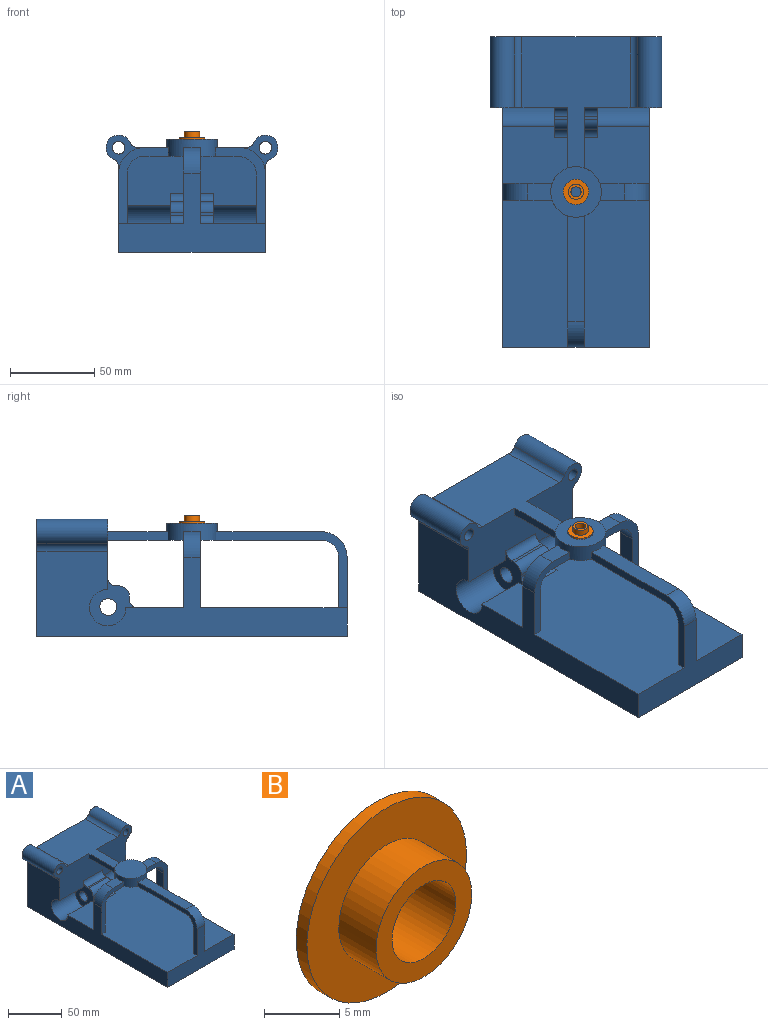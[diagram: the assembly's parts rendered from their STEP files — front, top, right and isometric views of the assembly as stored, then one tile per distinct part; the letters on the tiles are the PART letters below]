
ASSEMBLY  parts=2 mates=2
PART A: 49 faces, bbox 102x184x69.5 mm
  f0: plane 35.86x5mm, normal (1,0,0), area 179.3mm2, adj f4,f19,f30,f47
  f1: plane 35.86x5mm, normal (-1,0,0), area 179.3mm2, adj f4,f19,f30,f47
  f2: plane 62.86x10mm, normal (0,0,1), area 622.8mm2, adj f5,f6,f31,f47
  f3: plane 14.36x10mm, normal (0,0,1), area 137.8mm2, adj f7,f8,f41,f47
  f4: plane 77.86x64.09mm, normal (0,0,1), area 3044.5mm2, adj f0,f1,f15,f19,f38,f40,f47
  f5: plane 77.86x45mm, normal (1,0,0), area 562.5mm2, adj f2,f11,f17,f29,f30,f31,f32,f47
  f6: plane 77.86x45mm, normal (-1,0,0), area 562.5mm2, adj f2,f11,f17,f29,f30,f31,f32,f47
  f7: plane 45x29.36mm, normal (0,-1,0), area 320mm2, adj f3,f11,f16,f30,f41,f42,f43,f47
  f8: plane 45x29.36mm, normal (0,1,0), area 320mm2, adj f3,f11,f16,f30,f41,f42,f43,f47
  f9: plane 45x29.36mm, normal (0,-1,0), area 328.3mm2, adj f11,f12,f13,f30,f44,f45,f46,f47
  f10: plane 45x29.36mm, normal (0,1,0), area 328.3mm2, adj f11,f12,f13,f30,f44,f45,f46,f47
  f11: plane 131.18x87mm, normal (0,0,1), area 11087.4mm2, adj f5,f6,f7,f8,f9,f10,f12,f14
  f12: plane 184x50.54mm, normal (1,0,0), area 4560.9mm2, adj f9,f10,f11,f15,f17,f18,f19,f20
  f13: plane 14.36x10mm, normal (0,0,1), area 137.8mm2, adj f9,f10,f46,f47
  f14: cylinder r=10.82mm len=31mm, axis (1,0,0), area 1581mm2, adj f11,f16,f19,f24
  f15: plane 102x69.5mm, normal (0,1,0), area 5581mm2, adj f4,f12,f16,f18,f33,f34,f35,f36
  f16: plane 184x50.54mm, normal (-1,0,0), area 4560.9mm2, adj f7,f8,f11,f14,f15,f17,f18,f19
  f17: plane 87x47mm, normal (0,-1,0), area 1779mm2, adj f5,f6,f11,f12,f16,f18,f31
  f18: plane 184x87mm, normal (0,0,-1), area 16008mm2, adj f12,f15,f16,f17
  f19: plane 102x41.68mm, normal (0,-1,0), area 2935.5mm2, adj f0,f1,f4,f12,f14,f16,f20,f23
  f20: cylinder r=10.82mm len=31mm, axis (1,0,0), area 1581mm2, adj f11,f12,f19,f23
  f21: plane 25x1.82mm, normal (0,0,1), area 45.6mm2, adj f23,f24,f26,f27
  f22: plane 25x1.82mm, normal (0,-1,0), area 45.6mm2, adj f23,f24,f25,f27
  f23: plane 28.65x28.65mm, normal (1,0,0), area 364.8mm2, adj f11,f19,f20,f21,f22,f25,f26,f27
  f24: plane 28.65x28.65mm, normal (-1,0,0), area 364.8mm2, adj f11,f14,f19,f21,f22,f25,f26,f27
  f25: cylinder r=5mm len=25mm, axis (-1,0,0), area 196.3mm2, adj f11,f22,f23,f24
  f26: cylinder r=5mm len=25mm, axis (1,0,0), area 196.3mm2, adj f19,f21,f23,f24
  f27: cylinder r=6mm len=25mm, axis (1,0,0), area 235.6mm2, adj f21,f22,f23,f24
  f28: cylinder r=5mm len=25mm, axis (1,0,0), area 785.4mm2, adj f23,f24
  f29: cylinder r=10mm len=10mm, axis (-1,0,0), area 157.1mm2, adj f5,f6,f30,f32
  f30: plane 127x55.21mm, normal (0,0,-1), area 1940.2mm2, adj f0,f1,f5,f6,f7,f8,f9,f10
  f31: cylinder r=15mm len=15mm, axis (-1,0,0), area 235.6mm2, adj f2,f5,f6,f17
  f32: plane 30x10mm, normal (0,1,0), area 300mm2, adj f5,f6,f11,f29
  f33: cylinder r=7.5mm len=42mm, axis (0,-1,0), area 1225.1mm2, adj f15,f19,f39,f40
  f34: cylinder r=3.75mm len=42mm, axis (0,-1,0), area 989.6mm2, adj f15,f19
  f35: cylinder r=7.5mm len=42mm, axis (0,-1,0), area 1225.1mm2, adj f15,f19,f37,f38
  f36: cylinder r=3.75mm len=42mm, axis (0,-1,0), area 989.6mm2, adj f15,f19
  f37: cylinder r=5mm len=42mm, axis (0,-1,0), area 243.4mm2, adj f12,f15,f19,f35
  f38: cylinder r=5mm len=42mm, axis (0,-1,0), area 243.4mm2, adj f4,f15,f19,f35
  f39: cylinder r=5mm len=42mm, axis (0,-1,0), area 243.4mm2, adj f15,f16,f19,f33
  f40: cylinder r=5mm len=42mm, axis (0,-1,0), area 243.4mm2, adj f4,f15,f19,f33
  f41: cylinder r=15mm len=15mm, axis (0,1,0), area 235.6mm2, adj f3,f7,f8,f16
  f42: cylinder r=10mm len=10mm, axis (0,1,0), area 157.1mm2, adj f7,f8,f30,f43
  f43: plane 30x10mm, normal (1,0,0), area 300mm2, adj f7,f8,f11,f42
  f44: cylinder r=11.79mm len=11.79mm, axis (0,1,0), area 185.2mm2, adj f9,f10,f30,f45
  f45: plane 28.21x10mm, normal (-1,0,0), area 282.1mm2, adj f9,f10,f11,f44
  f46: cylinder r=15mm len=15mm, axis (0,1,0), area 235.6mm2, adj f9,f10,f12,f13
  f47: cylinder r=15mm len=30mm, axis (0,0,-1), area 738.6mm2, adj f0,f1,f2,f3,f4,f5,f6,f7
  f48: plane 30x30mm, normal (0,0,1), area 706.9mm2, adj f47
PART B: 6 faces, bbox 15x4.5x15 mm
  f0: cylinder r=7.5mm len=15mm, axis (0,1,0), area 47.1mm2, adj f1,f2
  f1: plane 15x15mm, normal (0,-1,0), area 113.1mm2, adj f0,f3
  f2: plane 15x15mm, normal (0,1,0), area 148.4mm2, adj f0,f5
  f3: cylinder r=4.5mm len=9mm, axis (0,1,0), area 99mm2, adj f1,f4
  f4: plane 9x9mm, normal (0,-1,0), area 35.3mm2, adj f3,f5
  f5: cylinder r=3mm len=6mm, axis (0,-1,0), area 84.8mm2, adj f2,f4
PLACE A t=(-3.33,10.19,1.15)mm
PLACE B rot(axis=(-1,0,0),90deg) t=(-3.33,10.19,68.15)mm
MATE planar B.f0 <-> A.f47  axis (0,0,-1) through (-3.33,10.19,68.15)mm
MATE cylindrical A.f47 <-> B.f3  axis (0,0,-1) through (-3.33,10.19,63.15)mm
